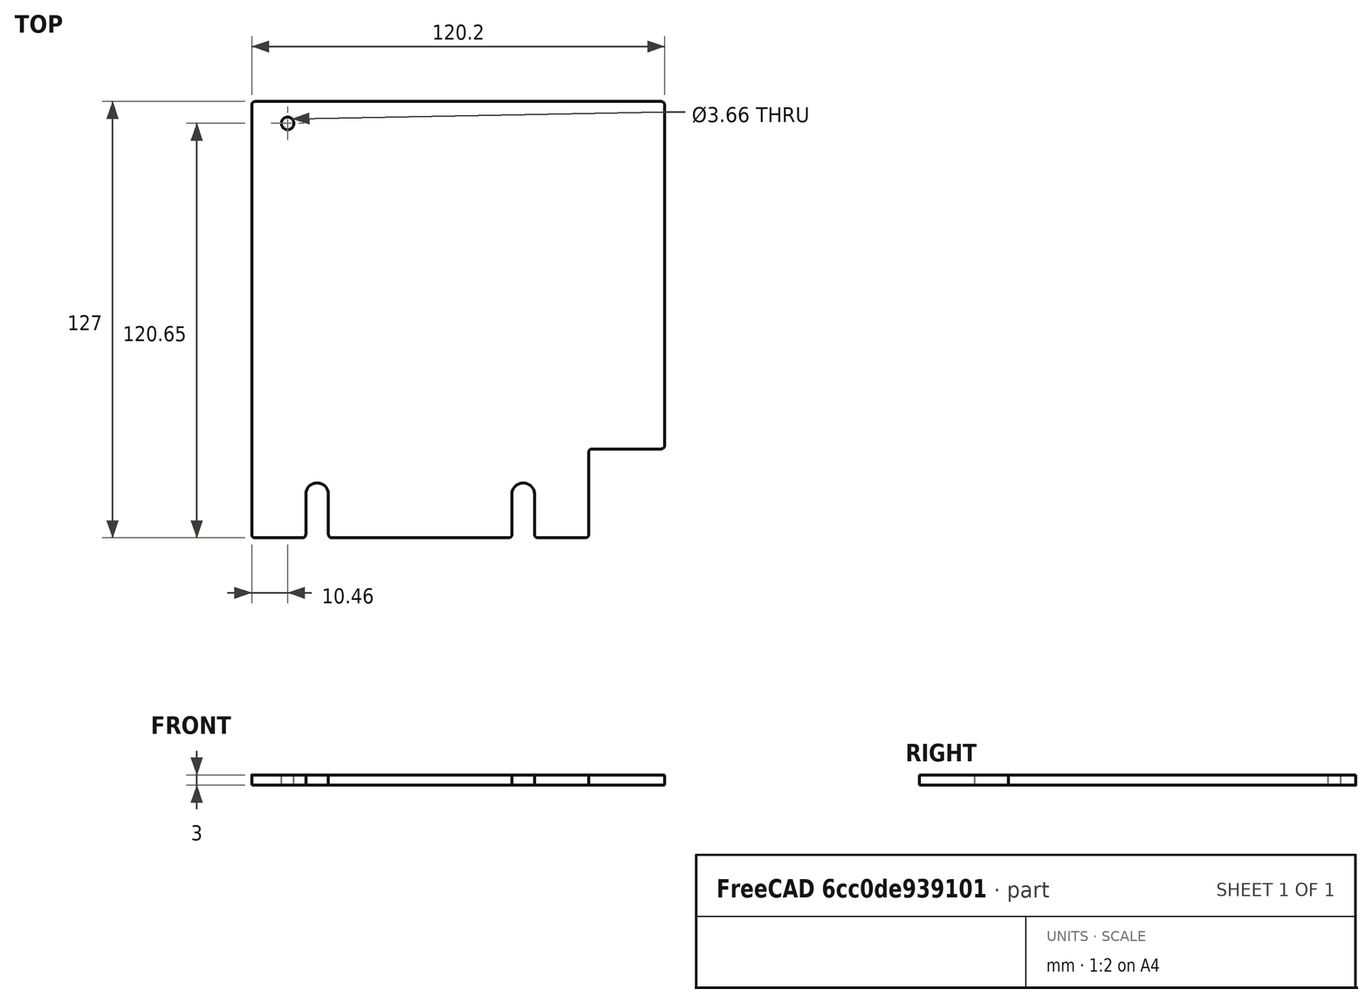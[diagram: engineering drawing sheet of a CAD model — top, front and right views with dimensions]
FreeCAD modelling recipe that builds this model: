
FCSTD DOCUMENT  (FreeCAD 0.21R33675 (Git))
Label: right_wall_back_5in
License: All rights reserved
LicenseURL: http://en.wikipedia.org/wiki/All_rights_reserved
objects: Spreadsheet::Sheet×1, Sketcher::SketchObject×1, PartDesign::Pad×1, PartDesign::Body×1
note: 4 computed .brp shape members not serialized (recipe doc carries the construction recipe); baked Part::Feature solids carry a one-line shape summary decoded from their .brp

FEATURE [Spreadsheet::Sheet] Spreadsheet
  cells = A2='Parameters; A3='ServoOffsetFromCenter; B3(ServoOffsetFromCenter)==-3 in; A4='BeamLength; B4(BeamLength)==18 in; A5='BracketLength; B5(BracketLength)==108.6 mm; A6='DistanceLeftBracketEdgeToDoor; B6(DistanceLeftBracketEdgeToDoor)==82.4999 mm; A7='DistanceRightBracketEdgeToDoor; B7(DistanceRightBracketEdgeToDoor)==23.1001 mm; A8='DoorMargin; B8(DoorMargin)==1 mm; A9='LengthMargin; B9(LengthMargin)==0 mm; A10='LengthLeftBracketEdgeToDoorGap; B10(LengthLeftBracketEdgeToDoorGap)==DistanceLeftBracketEdgeToDoor - DoorMargin; A11='LengthRightBracketEdgeToDoorGap; B11(LengthRightBracketEdgeToDoorGap)==DistanceRightBracketEdgeToDoor - DoorMargin; A12='LengthDoorGap; B12(LengthDoorGap)==BracketLength - LengthLeftBracketEdgeToDoorGap - LengthRightBracketEdgeToDoorGap; A13='BeamLengthMinusBracketLength; B13(BeamLengthMinusBracketLength)==BeamLength - BracketLength; A14='DistanceBackToDoor; B14(DistanceBackToDoor)==0.5 * BeamLengthMinusBracketLength + LengthRightBracketEdgeToDoorGap + ServoOffsetFromCenter; A15='DistanceBackToBracket; B15(DistanceBackToBracket)==0.5 * BeamLengthMinusBracketLength + ServoOffsetFromCenter; A16='LengthBackToDoor; B16(LengthBackToDoor)==DistanceBackToDoor - LengthMargin; A17='LengthBackToBracket; B17(LengthBackToBracket)==DistanceBackToBracket - LengthMargin; A18='Height; B18(Height)==5 in; A19='Thickness; B19(Thickness)==3 mm; A20='CutoutMargin; B20(CutoutMargin)==0.5 mm; A21='CutoutHeight; B21(CutoutHeight)==1 in + CutoutMargin; A22='FilletRadius; B22(FilletRadius)==1 mm; A23='MountHoleDiameter; B23(MountHoleDiameter)==0.26 in; A24='MountHoleDistanceFromBottom; B24(MountHoleDistanceFromBottom)==0.5 in; A25='MountHoleSideMargin; B25(MountHoleSideMargin)==0.75 in; A27='RABracketWidth; B27(RABracketWidth)==0.5 in; A28='RABracketHoleDiameter; B28(RABracketHoleDiameter)==0.144 in; A29='RABracketHoleOffset; B29(RABracketHoleOffset)==0.412 in; A30='RAUpperBracketHoleFromTop; B30(RAUpperBracketHoleFromTop)==0.5 * RABracketWidth; A31='RABracketHoleFromSide; B31(RABracketHoleFromSide)==RABracketHoleOffset
FEATURE [Sketcher::SketchObject] Sketch
  FullyConstrained = true
  MapMode = 5
  Support = -> [XY_Plane]
  expr: Constraints[103] = Spreadsheet.RAUpperBracketHoleFromTop
  expr: Constraints[105] = Spreadsheet.RABracketHoleDiameter
  expr: Constraints[14] = Spreadsheet.FilletRadius
  expr: Constraints[20] = Spreadsheet.Height
  expr: Constraints[43] = Spreadsheet.MountHoleDistanceFromBottom
  expr: Constraints[44] = Spreadsheet.MountHoleDiameter
  expr: Constraints[59] = Spreadsheet.MountHoleSideMargin
  expr: Constraints[7] = Spreadsheet.LengthBackToDoor
  expr: Constraints[8] = Spreadsheet.LengthBackToBracket
  expr: Constraints[9] = Spreadsheet.CutoutHeight
  sketch-geometry (43):
    g0: LineSegment StartX=0 StartY=126 StartZ=0 EndX=0 EndY=1 EndZ=0
    g1: LineSegment StartX=1 StartY=0 StartZ=0 EndX=97.1 EndY=0 EndZ=0
    g2: LineSegment StartX=98.1 StartY=1 StartZ=0 EndX=98.1 EndY=24.9 EndZ=0
    g3: LineSegment StartX=99.1 StartY=25.9 StartZ=0 EndX=119.2 EndY=25.9 EndZ=0
    g4: LineSegment StartX=120.2 StartY=26.9 StartZ=0 EndX=120.2 EndY=126 EndZ=0
    g5: LineSegment StartX=119.2 StartY=127 StartZ=0 EndX=1 EndY=127 EndZ=0
    g6: ArcOfCircle CenterX=1 CenterY=126 CenterZ=0 NormalX=0 NormalY=0 NormalZ=1 AngleXU=0 Radius=1 StartAngle=1.5708 EndAngle=3.14159
    g7: GeomPoint X=0 Y=127 Z=0
    g8: ArcOfCircle CenterX=1 CenterY=1 CenterZ=0 NormalX=0 NormalY=0 NormalZ=1 AngleXU=0 Radius=1 StartAngle=3.14159 EndAngle=4.71239
    g9: GeomPoint X=0 Y=0 Z=0
    g10: ArcOfCircle CenterX=97.1 CenterY=1 CenterZ=0 NormalX=0 NormalY=0 NormalZ=1 AngleXU=0 Radius=1 StartAngle=4.71239 EndAngle=6.28319
    g11: GeomPoint X=98.1 Y=0 Z=0
    g12: ArcOfCircle CenterX=99.1 CenterY=24.9 CenterZ=0 NormalX=0 NormalY=0 NormalZ=1 AngleXU=0 Radius=1 StartAngle=1.5708 EndAngle=3.14159
    g13: GeomPoint X=98.1 Y=25.9 Z=0
    g14: ArcOfCircle CenterX=119.2 CenterY=26.9 CenterZ=0 NormalX=0 NormalY=0 NormalZ=1 AngleXU=0 Radius=1 StartAngle=4.71239 EndAngle=6.28319
    g15: GeomPoint X=120.2 Y=25.9 Z=0
    g16: ArcOfCircle CenterX=119.2 CenterY=126 CenterZ=0 NormalX=0 NormalY=0 NormalZ=1 AngleXU=0 Radius=1 StartAngle=-5.977e-13 EndAngle=1.5708
    g17: GeomPoint X=120.2 Y=127 Z=0
    g18: GeomPoint X=19.05 Y=0 Z=0
    g19: LineSegment StartX=19.05 StartY=0 StartZ=0 EndX=19.05 EndY=12.7 EndZ=0
    g20: Circle CenterX=19.05 CenterY=12.7 CenterZ=0 NormalX=0 NormalY=0 NormalZ=1 AngleXU=0 Radius=3.302
    g21: LineSegment StartX=79.05 StartY=12.7 StartZ=0 EndX=79.05 EndY=0 EndZ=0
    g22: LineSegment StartX=79.05 StartY=12.7 StartZ=0 EndX=98.1 EndY=12.7 EndZ=0
    g23: LineSegment StartX=19.05 StartY=12.7 StartZ=0 EndX=0 EndY=12.7 EndZ=0
    g24: Circle CenterX=79.05 CenterY=12.7 CenterZ=0 NormalX=0 NormalY=0 NormalZ=1 AngleXU=0 Radius=3.302
    g25: ArcOfCircle CenterX=19.05 CenterY=12.7 CenterZ=0 NormalX=0 NormalY=0 NormalZ=1 AngleXU=0 Radius=3.302 StartAngle=0 EndAngle=3.14159
    g26: LineSegment StartX=19.05 StartY=12.7 StartZ=0 EndX=22.352 EndY=12.7 EndZ=0
    g27: LineSegment StartX=15.748 StartY=12.7 StartZ=0 EndX=15.748 EndY=1 EndZ=0
    g28: LineSegment StartX=22.352 StartY=12.7 StartZ=0 EndX=22.352 EndY=1 EndZ=0
    g29: ArcOfCircle CenterX=14.748 CenterY=1 CenterZ=0 NormalX=0 NormalY=0 NormalZ=1 AngleXU=0 Radius=1 StartAngle=4.71239 EndAngle=6.28319
    g30: ArcOfCircle CenterX=23.352 CenterY=1 CenterZ=0 NormalX=0 NormalY=0 NormalZ=1 AngleXU=0 Radius=1 StartAngle=3.14159 EndAngle=4.71239
    g31: ArcOfCircle CenterX=79.05 CenterY=12.7 CenterZ=0 NormalX=0 NormalY=0 NormalZ=1 AngleXU=0 Radius=3.302 StartAngle=-1.8e-15 EndAngle=3.14159
    g32: LineSegment StartX=79.05 StartY=12.7 StartZ=0 EndX=75.748 EndY=12.7 EndZ=0
    g33: LineSegment StartX=75.748 StartY=12.7 StartZ=0 EndX=75.748 EndY=1 EndZ=0
    g34: LineSegment StartX=82.352 StartY=12.7 StartZ=0 EndX=82.352 EndY=1 EndZ=0
    g35: ArcOfCircle CenterX=74.748 CenterY=1 CenterZ=0 NormalX=0 NormalY=0 NormalZ=1 AngleXU=0 Radius=1 StartAngle=4.71239 EndAngle=6.28319
    g36: ArcOfCircle CenterX=83.352 CenterY=1 CenterZ=0 NormalX=0 NormalY=0 NormalZ=1 AngleXU=0 Radius=1 StartAngle=3.14159 EndAngle=4.71239
    g37: LineSegment StartX=83.352 StartY=0 StartZ=0 EndX=97.1 EndY=0 EndZ=0
    g38: LineSegment StartX=23.352 StartY=0 StartZ=0 EndX=74.748 EndY=0 EndZ=0
    g39: LineSegment StartX=1 StartY=0 StartZ=0 EndX=14.748 EndY=0 EndZ=0
    g40: LineSegment StartX=0 StartY=127 StartZ=0 EndX=10.46 EndY=127 EndZ=0
    g41: LineSegment StartX=10.46 StartY=127 StartZ=0 EndX=10.46 EndY=120.65 EndZ=0
    g42: Circle CenterX=10.46 CenterY=120.65 CenterZ=0 NormalX=0 NormalY=0 NormalZ=1 AngleXU=0 Radius=1.8288
  constraints (106):
    c: Vertical(g0)
    c: Horizontal(g1)
    c: Vertical(g2)
    c: Horizontal(g3)
    c: Vertical(g4)
    c: Horizontal(g5)
    c: Coincident(g-1,g9)
    c: DistanceX(g7,g17) = 120.2
    c: DistanceX(g9,g11) = 98.1
    c: DistanceY(g11,g13) = 25.9
    c: PointOnObject(g7,g0)
    c: PointOnObject(g7,g5)
    c: Tangent(g0,g6) = -1.5708
    c: Tangent(g5,g6) = -1.5708
    c: Radius(g6) = 1
    c: PointOnObject(g9,g0)
    c: PointOnObject(g9,g1)
    c: Tangent(g0,g8) = -1.5708
    c: Tangent(g1,g8) = -1.5708
    c: Equal(g8,g6)
    c: DistanceY(g1,g5) = 127
    c: PointOnObject(g11,g1)
    c: PointOnObject(g11,g2)
    c: Tangent(g1,g10) = -1.5708
    c: Tangent(g2,g10) = -1.5708
    c: Equal(g10,g8)
    c: PointOnObject(g13,g2)
    c: PointOnObject(g13,g3)
    c: Tangent(g2,g12) = 1.5708
    c: Tangent(g3,g12) = 1.5708
    c: Equal(g12,g10)
    c: PointOnObject(g15,g3)
    c: PointOnObject(g15,g4)
    c: Tangent(g3,g14) = -1.5708
    c: Tangent(g4,g14) = -1.5708
    c: Equal(g14,g12)
    c: PointOnObject(g17,g5)
    c: PointOnObject(g17,g4)
    c: Tangent(g5,g16) = -1.5708
    c: Tangent(g4,g16) = -1.5708
    c: Equal(g16,g14)
    c: Coincident(g19,g18)
    c: Vertical(g19)
    c: DistanceY(g19,g19) = 12.7
    c: Diameter(g20) = 6.604
    c: Coincident(g20,g19)
    c: PointOnObject(g18,g1)
    c: PointOnObject(g21,g1)
    c: Vertical(g21)
    c: Equal(g19,g21)
    c: Coincident(g22,g21)
    c: PointOnObject(g22,g2)
    c: Horizontal(g22)
    c: Coincident(g23,g20)
    c: PointOnObject(g23,g0)
    c: Horizontal(g23)
    c: Equal(g23,g22)
    c: Coincident(g24,g21)
    c: Equal(g24,g20)
    c: DistanceX(g23,g23) = 19.05
    c: Coincident(g25,g19)
    c: PointOnObject(g25,g23)
    c: Coincident(g26,g25)
    c: Coincident(g26,g25)
    c: Horizontal(g26)
    c: PointOnObject(g25,g20)
    c: Coincident(g27,g25)
    c: Vertical(g27)
    c: Coincident(g28,g25)
    c: Vertical(g28)
    c: Equal(g27,g28)
    c: Tangent(g29,g27) = 1.5708
    c: Tangent(g29,g1) = -1.5708
    c: Tangent(g30,g28) = -1.5708
    c: Tangent(g30,g1) = -1.5708
    c: Equal(g29,g8)
    c: Coincident(g31,g21)
    c: PointOnObject(g31,g22)
    c: Coincident(g32,g31)
    c: Coincident(g32,g31)
    c: Horizontal(g32)
    c: PointOnObject(g31,g24)
    c: Coincident(g33,g31)
    c: Vertical(g33)
    c: Coincident(g34,g31)
    c: Vertical(g34)
    c: Equal(g33,g34)
    c: Tangent(g35,g33) = 1.5708
    c: Tangent(g35,g1) = -1.5708
    c: Tangent(g36,g34) = -1.5708
    c: Tangent(g36,g1) = -1.5708
    c: Equal(g36,g10)
    c: Coincident(g37,g36)
    c: Coincident(g37,g10)
    c: Coincident(g38,g30)
    c: Coincident(g38,g35)
    c: Coincident(g39,g8)
    c: Coincident(g39,g29)
    c: Horizontal(g40)
    c: Coincident(g7,g40)
    c: DistanceX(g40,g40) = 10.46
    c: Coincident(g41,g40)
    c: Vertical(g41)
    c: DistanceY(g41,g41) = 6.35
    c: Coincident(g42,g41)
    c: Diameter(g42) = 3.6576
FEATURE [PartDesign::Pad] Pad
  Direction = (0,0,1)
  Length = 3
  Length2 = 10
  Profile = -> Sketch
  ReferenceAxis = -> Sketch [N_Axis]
  Type = 0
  expr: Length = Spreadsheet.Thickness
FEATURE [PartDesign::Body] Body
  Group = -> [Sketch,Pad]
  Origin = -> Origin
  Tip = -> Pad
